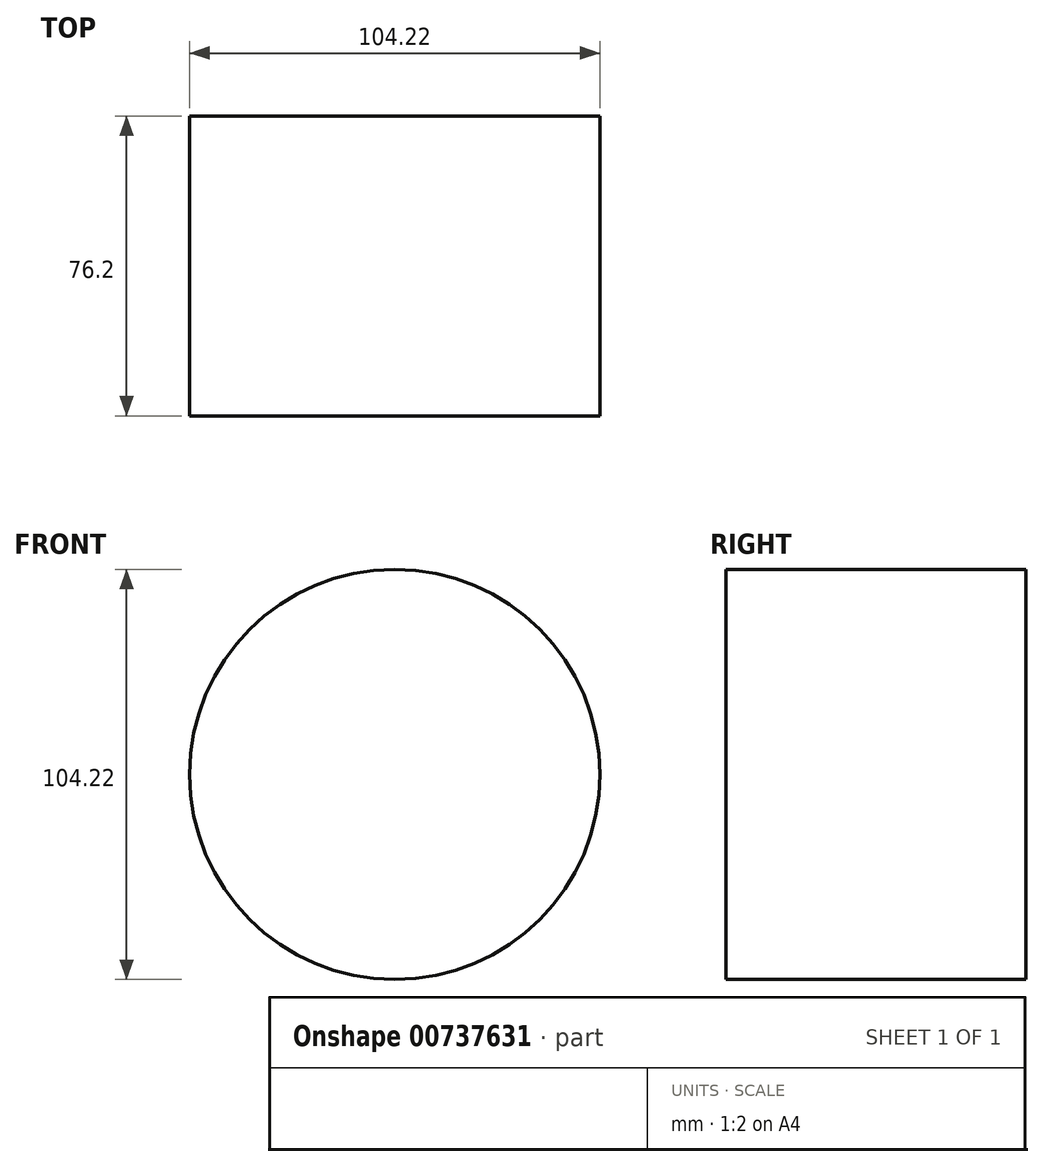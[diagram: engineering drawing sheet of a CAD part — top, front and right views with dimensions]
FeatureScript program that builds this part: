
annotation { "Feature Type Name" : "Feature", "Feature Type Description" : "" }
export const myFeature = defineFeature(function(context is Context, id is Id, definition is map)
    precondition{}
    {
        {
            var Q0;
            Q0=qCreatedBy(makeId("Front.planeOp"),FACE);
            var sketch = newSketch(context, id + "F0", { "sketchPlane" : qUnion([Q0])});
            skCircle(sketch, "E0", {"center": v(0, 0) * mm, "radius": 52.53 * mm});
            skSolve(sketch);
        }
        {
            var Q0;
            Q0=makeQuery(id+"F0.imprint","IMPRINT",FACE,{"disambiguationData":[TD([[makeQuery(id+"F0.imprint","IMPRINT",EDGE,{"derivedFrom":sQuery(id+"F0.wireOp",EDGE,"E0")}),1.0]])]});
            var sketch = newSketch(context, id + "F1", { "sketchPlane" : qUnion([Q0])});
            skCircle(sketch, "E1", {"center": v(0, 0) * mm, "radius": 52.11 * mm});
            skSolve(sketch);
        }
        {
            var Q0;
            Q0=makeQuery(id+"F1.imprint","IMPRINT",FACE,{"disambiguationData":[TD([[makeQuery(id+"F1.imprint","IMPRINT",EDGE,{"derivedFrom":sQuery(id+"F1.wireOp",EDGE,"E1")}),1.0]])]});
            extrude(context, id + "F2", {"entities" : qUnion([Q0]), "depth" : 76.2 * mm, "offsetDistance" : 25.4 * mm});
        }
        {
            var Q0;
            Q0 = qSketchRegion(id + "F0", true);
            var sketch = newSketch(context, id + "F3", { "sketchPlane" : qUnion([Q0])});
            skCircle(sketch, "E2", {"center": v(0, 0) * mm, "radius": 50.48 * mm});
            skSolve(sketch);
        }
        {
            var Q0;
            Q0 = qSketchRegion(id + "F3", true);
            extrude(context, id + "F4", {"entities" : qUnion([Q0]), "operationType" : NewBodyOperationType.ADD, "depth" : 76.2 * mm, "offsetDistance" : 25.4 * mm});
        }
    });
